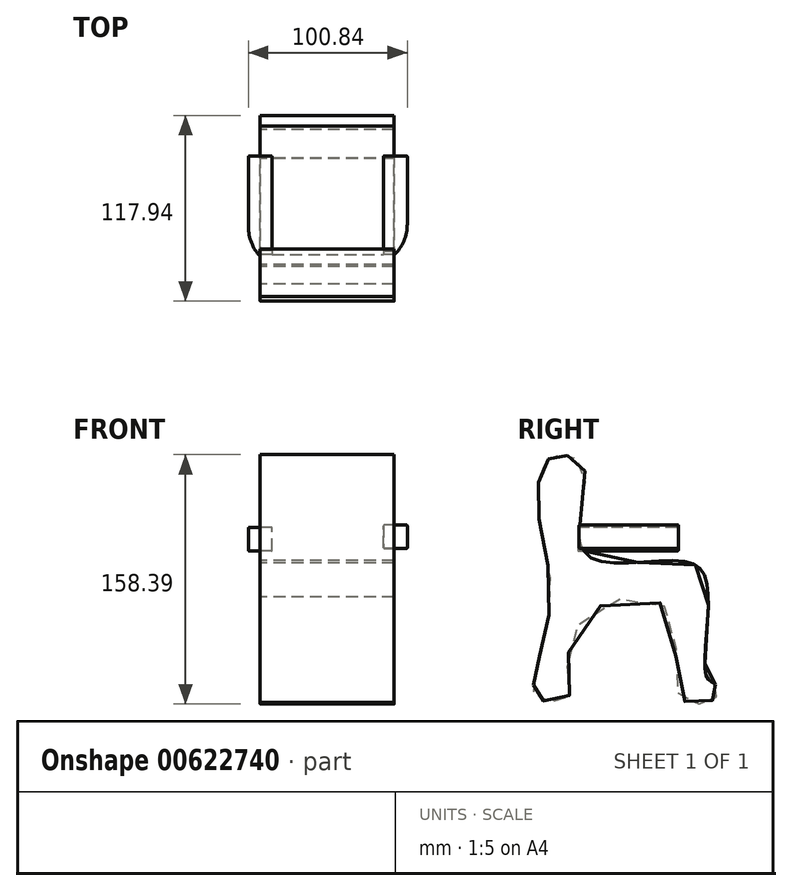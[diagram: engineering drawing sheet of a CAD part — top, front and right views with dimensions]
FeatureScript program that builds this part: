
annotation { "Feature Type Name" : "Feature", "Feature Type Description" : "" }
export const myFeature = defineFeature(function(context is Context, id is Id, definition is map)
    precondition{}
    {
        {
            var Q0;
            Q0=qCreatedBy(makeId("Right.planeOp"),FACE);
            var sketch = newSketch(context, id + "F0", { "sketchPlane" : qUnion([Q0])});
            skFitSpline(sketch, "E0", {"points": [v(-40.08, 10.5) * mm, v(-40.67, 59.9) * mm, v(-47.18, 71.44) * mm, v(-54.57, 73.5) * mm, v(-60.2, 73.21) * mm, v(-67.3, 67.6) * mm, v(-70.55, 54.58) * mm, v(-69.66, 30.32) * mm, v(-62.86, -9.9) * mm, v(-67.88, -47.48) * mm, v(-72.91, -66.11) * mm, v(-73.8, -76.17) * mm, v(-71.73, -81.2) * mm, v(-52.8, -82.68) * mm, v(-51.02, -74.4) * mm, v(-42.15, -30.32) * mm, v(11.1, -24.12) * mm, v(18.5, -78.84) * mm, v(32.99, -84.46) * mm, v(42.16, -80.62) * mm, v(43.93, -74.7) * mm, v(39.8, -70.86) * mm, v(35.65, -65.24) * mm, v(37.13, -12.88) * mm, v(22.04, 6.06) * mm, v(-40.08, 10.5) * mm]});
            skSolve(sketch);
        }
        {
            var Q0;
            Q0=makeQuery(id+"F0.imprint","IMPRINT",FACE,{"disambiguationData":[TD([[makeQuery(id+"F0.imprint","IMPRINT",EDGE,{"derivedFrom":sQuery(id+"F0.wireOp",EDGE,"E0")}),1.0]])]});
            extrude(context, id + "F1", {"entities" : qUnion([Q0]), "endBound" : BoundingType.SYMMETRIC, "depth" : 85 * mm, "offsetDistance" : 25.4 * mm});
        }
        {
            var Q0;
            Q0=qCreatedBy(makeId("Front.planeOp"),FACE);
            cPlane(context, id + "F2", {"entities" : qUnion([Q0]), "cplaneType" : CPlaneType.OFFSET, "offset" : 44.7 * mm, "width" : 150 * mm, "height" : 150 * mm});
        }
        {
            var Q0;
            Q0=qCreatedBy(id+"F2.planeOp",FACE);
            var sketch = newSketch(context, id + "F3", { "sketchPlane" : qUnion([Q0])});
            skLineSegment(sketch, "E1.bottom", {"start": v(35.92, 14.07) * mm, "end": v(50.92, 14.07) * mm});
            skLineSegment(sketch, "E1.top", {"start": v(35.92, 29.07) * mm, "end": v(50.92, 29.07) * mm});
            skLineSegment(sketch, "E1.left", {"start": v(35.92, 14.07) * mm, "end": v(35.92, 29.07) * mm});
            skLineSegment(sketch, "E1.right", {"start": v(50.92, 14.07) * mm, "end": v(50.92, 29.07) * mm});
            skPoint(sketch, "E1.middle", {"position": v(43.42, 21.57) * mm});
            skSolve(sketch);
        }
        {
            var Q0;
            Q0=qCreatedBy(makeId("Right.planeOp"),FACE);
            cPlane(context, id + "F4", {"entities" : qUnion([Q0]), "cplaneType" : CPlaneType.OFFSET, "offset" : 42.2 * mm, "width" : 150 * mm, "height" : 150 * mm});
        }
        {
            var Q0;
            Q0=qCreatedBy(id+"F4.planeOp",FACE);
            var sketch = newSketch(context, id + "F5", { "sketchPlane" : qUnion([Q0])});
            skLineSegment(sketch, "E2", {"start": v(-44.72, 21.27) * mm, "end": v(18.5, 21.27) * mm});
            skSolve(sketch);
        }
        {
            var Q0;
            Q0=makeQuery(id+"F3.imprint","IMPRINT",FACE,{"disambiguationData":[TD([[makeQuery(id+"F3.imprint","IMPRINT",EDGE,{"derivedFrom":sQuery(id+"F3.wireOp",EDGE,"E1.bottom")}),1.0]])]});
            var Q1;
            Q1 = qConstructionFilter(qBodyType(qCreatedBy(id + "F5" ,EDGE), BodyType.WIRE), ConstructionObject.NO);
            sweep(context, id + "F6", {"operationType" : NewBodyOperationType.ADD, "profiles" : qUnion([Q0]), "path" : qUnion([Q1])});
        }
        {
            var Q0;
            Q0=makeQuery(id+"F6.opSweep","CAP_EDGE",EDGE,{"disambiguationData":[OSD([sQuery(id+"F3.wireOp",EDGE,"E1.right"),sQuery(id+"F5.wireOp",VERTEX,"E2.start")])],"isStart":false});
            fillet(context, id + "F7", {"entities" : qUnion([Q0]), "radius" : 28 * mm, "tangentPropagation" : true, "allowEdgeOverflow" : false});
        }
        {
            var Q0;
            Q0=qCreatedBy(makeId("Right.planeOp"),FACE);
            cPlane(context, id + "F8", {"entities" : qUnion([Q0]), "cplaneType" : CPlaneType.OFFSET, "offset" : 42.2 * mm, "oppositeDirection" : true, "width" : 150 * mm, "height" : 150 * mm});
        }
        {
            var Q0;
            Q0=qCreatedBy(id+"F2.planeOp",FACE);
            var sketch = newSketch(context, id + "F9", { "sketchPlane" : qUnion([Q0])});
            skLineSegment(sketch, "E3.bottom", {"start": v(-34.92, 27.46) * mm, "end": v(-49.92, 27.46) * mm});
            skLineSegment(sketch, "E3.top", {"start": v(-34.92, 12.46) * mm, "end": v(-49.92, 12.46) * mm});
            skLineSegment(sketch, "E3.left", {"start": v(-34.92, 27.46) * mm, "end": v(-34.92, 12.46) * mm});
            skLineSegment(sketch, "E3.right", {"start": v(-49.92, 27.46) * mm, "end": v(-49.92, 12.46) * mm});
            skPoint(sketch, "E3.middle", {"position": v(-42.42, 19.96) * mm});
            skSolve(sketch);
        }
        {
            var Q0;
            Q0=qCreatedBy(id+"F8.planeOp",FACE);
            var sketch = newSketch(context, id + "F10", { "sketchPlane" : qUnion([Q0])});
            skLineSegment(sketch, "E4", {"start": v(18.3, 21.47) * mm, "end": v(-45.52, 21.47) * mm});
            skSolve(sketch);
        }
        {
            var Q0;
            Q0=makeQuery(id+"F9.imprint","IMPRINT",FACE,{"disambiguationData":[TD([[makeQuery(id+"F9.imprint","IMPRINT",EDGE,{"derivedFrom":sQuery(id+"F9.wireOp",EDGE,"E3.bottom")}),1.0]])]});
            var Q1;
            Q1 = qConstructionFilter(qBodyType(qCreatedBy(id + "F10" ,EDGE), BodyType.WIRE), ConstructionObject.NO);
            sweep(context, id + "F11", {"operationType" : NewBodyOperationType.ADD, "profiles" : qUnion([Q0]), "path" : qUnion([Q1])});
        }
        {
            var Q0;
            Q0=makeQuery(id+"F11.opSweep","CAP_EDGE",EDGE,{"disambiguationData":[OSD([sQuery(id+"F9.wireOp",EDGE,"E3.right"),sQuery(id+"F10.wireOp",VERTEX,"E4.end")])],"isStart":false});
            fillet(context, id + "F12", {"entities" : qUnion([Q0]), "radius" : 28 * mm, "tangentPropagation" : true, "allowEdgeOverflow" : false});
        }
        {
            var Q0;
            Q0=makeQuery(id+"F11.opSweep","SWEPT_EDGE",EDGE,{"disambiguationData":[OSD([sQuery(id+"F9.wireOp",EDGE,"E3.bottom"),sQuery(id+"F9.wireOp",EDGE,"E3.right"),sQuery(id+"F10.wireOp",EDGE,"E4")])]});
            var Q1;
            Q1=makeQuery(id+"F11.opSweep","SWEPT_EDGE",EDGE,{"disambiguationData":[OSD([sQuery(id+"F9.wireOp",EDGE,"E3.bottom"),sQuery(id+"F9.wireOp",EDGE,"E3.left"),sQuery(id+"F10.wireOp",EDGE,"E4")])]});
            var Q2;
            Q2=makeQuery(id+"F11.opSweep","CAP_EDGE",EDGE,{"disambiguationData":[OSD([sQuery(id+"F9.wireOp",EDGE,"E3.top"),sQuery(id+"F10.wireOp",VERTEX,"E4.start")])],"isStart":true});
            var Q3;
            Q3=makeQuery(id+"F11.opSweep","SWEPT_EDGE",EDGE,{"disambiguationData":[OSD([sQuery(id+"F9.wireOp",EDGE,"E3.top"),sQuery(id+"F9.wireOp",EDGE,"E3.right"),sQuery(id+"F10.wireOp",EDGE,"E4")])]});
            var Q4;
            Q4=makeQuery(id+"F11.opSweep","CAP_EDGE",EDGE,{"disambiguationData":[OSD([sQuery(id+"F9.wireOp",EDGE,"E3.right"),sQuery(id+"F10.wireOp",VERTEX,"E4.start")])],"isStart":true});
            var Q5;
            Q5=makeQuery(id+"F11.opSweep","CAP_EDGE",EDGE,{"disambiguationData":[OSD([sQuery(id+"F9.wireOp",EDGE,"E3.left"),sQuery(id+"F10.wireOp",VERTEX,"E4.start")])],"isStart":true});
            var Q6;
            Q6=makeQuery(id+"F11.opSweep","CAP_EDGE",EDGE,{"disambiguationData":[OSD([sQuery(id+"F9.wireOp",EDGE,"E3.bottom"),sQuery(id+"F10.wireOp",VERTEX,"E4.start")])],"isStart":true});
            var Q7;
            Q7=makeQuery(id+"F11.opSweep","SWEPT_EDGE",EDGE,{"disambiguationData":[OSD([sQuery(id+"F9.wireOp",EDGE,"E3.top"),sQuery(id+"F9.wireOp",EDGE,"E3.left"),sQuery(id+"F10.wireOp",EDGE,"E4")])]});
            fillet(context, id + "F13", {"entities" : qUnion([Q0, Q1, Q2, Q3, Q4, Q5, Q6, Q7]), "radius" : 0.5 * mm, "tangentPropagation" : true, "allowEdgeOverflow" : false});
        }
        {
            var Q0;
            Q0=makeQuery(id+"F6.opSweep","SWEPT_EDGE",EDGE,{"disambiguationData":[OSD([sQuery(id+"F3.wireOp",EDGE,"E1.bottom"),sQuery(id+"F3.wireOp",EDGE,"E1.right"),sQuery(id+"F5.wireOp",EDGE,"E2")])]});
            var Q1;
            Q1=makeQuery(id+"F6.opSweep","SWEPT_EDGE",EDGE,{"disambiguationData":[OSD([sQuery(id+"F3.wireOp",EDGE,"E1.bottom"),sQuery(id+"F3.wireOp",EDGE,"E1.left"),sQuery(id+"F5.wireOp",EDGE,"E2")])]});
            var Q2;
            Q2=makeQuery(id+"F6.opSweep","CAP_EDGE",EDGE,{"disambiguationData":[OSD([sQuery(id+"F3.wireOp",EDGE,"E1.bottom"),sQuery(id+"F5.wireOp",VERTEX,"E2.end")])],"isStart":true});
            var Q3;
            Q3=makeQuery(id+"F6.opSweep","CAP_EDGE",EDGE,{"disambiguationData":[OSD([sQuery(id+"F3.wireOp",EDGE,"E1.top"),sQuery(id+"F5.wireOp",VERTEX,"E2.end")])],"isStart":true});
            var Q4;
            Q4=makeQuery(id+"F6.opSweep","CAP_EDGE",EDGE,{"disambiguationData":[OSD([sQuery(id+"F3.wireOp",EDGE,"E1.right"),sQuery(id+"F5.wireOp",VERTEX,"E2.end")])],"isStart":true});
            var Q5;
            Q5=makeQuery(id+"F6.opSweep","CAP_EDGE",EDGE,{"disambiguationData":[OSD([sQuery(id+"F3.wireOp",EDGE,"E1.left"),sQuery(id+"F5.wireOp",VERTEX,"E2.end")])],"isStart":true});
            var Q6;
            Q6=makeQuery(id+"F6.opSweep","SWEPT_EDGE",EDGE,{"disambiguationData":[OSD([sQuery(id+"F3.wireOp",EDGE,"E1.top"),sQuery(id+"F3.wireOp",EDGE,"E1.left"),sQuery(id+"F5.wireOp",EDGE,"E2")])]});
            var Q7;
            Q7=makeQuery(id+"F6.opSweep","SWEPT_EDGE",EDGE,{"disambiguationData":[OSD([sQuery(id+"F3.wireOp",EDGE,"E1.top"),sQuery(id+"F3.wireOp",EDGE,"E1.right"),sQuery(id+"F5.wireOp",EDGE,"E2")])]});
            fillet(context, id + "F14", {"entities" : qUnion([Q0, Q1, Q2, Q3, Q4, Q5, Q6, Q7]), "radius" : 0.5 * mm, "tangentPropagation" : true, "allowEdgeOverflow" : false});
        }
    });
